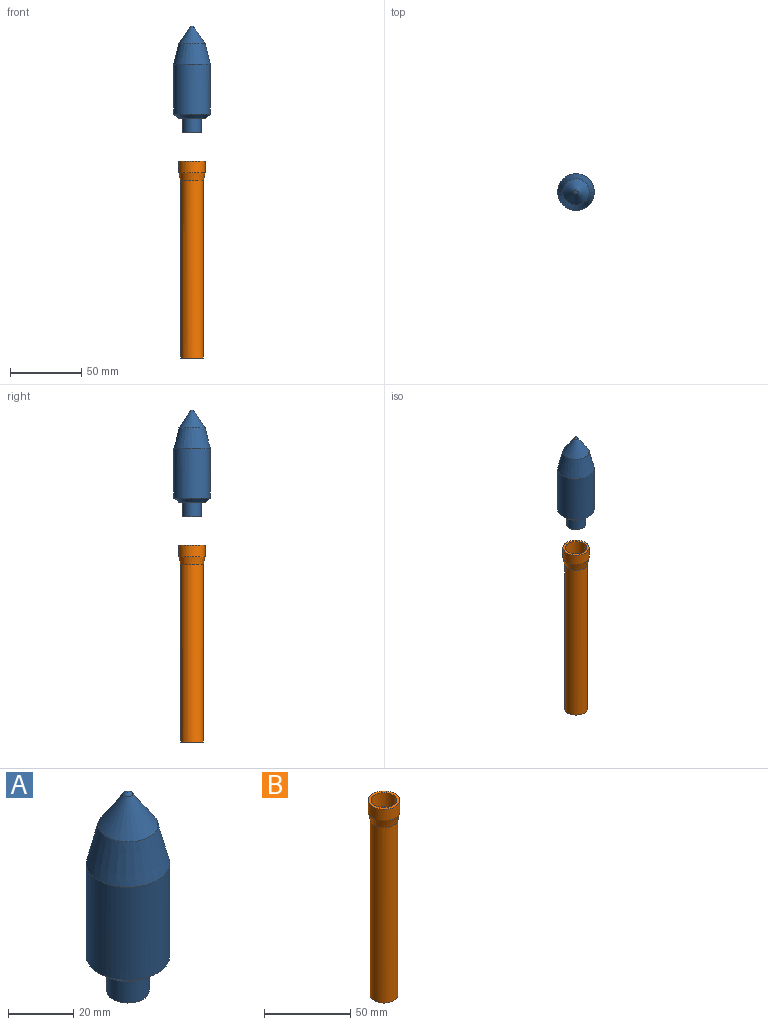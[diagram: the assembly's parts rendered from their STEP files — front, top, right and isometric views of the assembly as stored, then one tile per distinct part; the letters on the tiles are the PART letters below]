
ASSEMBLY  parts=2 mates=1
PART A: 8 faces, bbox 25.7x25.7x74.9 mm
  f0: sphere r=1.74mm, area 8.4mm2, adj f1
  f1: cone r=1.44mm half-angle=34deg, axis (0,0,-1), area 465.5mm2, adj f0,f2
  f2: cone r=9.22mm half-angle=14deg, axis (0,0,-1), area 1039.7mm2, adj f1,f3
  f3: cylinder r=12.85mm len=35mm, axis (0,0,-1), area 2824.9mm2, adj f2,f4
  f4: cone r=12.85mm half-angle=50deg, axis (0,0,1), area 328.3mm2, adj f3,f5
  f5: plane 18.43x18.43mm, normal (0,0,-1), area 134.2mm2, adj f4,f6
  f6: cylinder r=6.5mm len=13mm, axis (0,0,1), area 408.4mm2, adj f5,f7
  f7: plane 13x13mm, normal (0,0,-1), area 132.7mm2, adj f6
PART B: 8 faces, bbox 18.4x18.4x138.2 mm
  f0: cylinder r=7mm len=128.2mm, axis (0,0,-1), area 5638.4mm2, adj f6,f7
  f1: cylinder r=8.05mm len=124.52mm, axis (0,0,-1), area 6297.6mm2, adj f2,f7
  f2: cone r=9.22mm half-angle=11.7deg, axis (0,0,1), area 313mm2, adj f1,f3
  f3: cylinder r=9.22mm len=18.43mm, axis (0,0,-1), area 464.7mm2, adj f2,f4
  f4: plane 18.43x18.43mm, normal (0,0,1), area 90.2mm2, adj f3,f5
  f5: cylinder r=7.5mm len=15mm, axis (0,0,1), area 471.2mm2, adj f4,f6
  f6: plane 15x15mm, normal (0,0,1), area 22.8mm2, adj f0,f5
  f7: plane 16.1x16.1mm, normal (0,0,-1), area 49.6mm2, adj f0,f1
PLACE A t=(0,0,30)mm
PLACE B at identity
MATE slider B.f5 <-> A.f6  axis (0,0,1) through (0,0,223.74)mm
